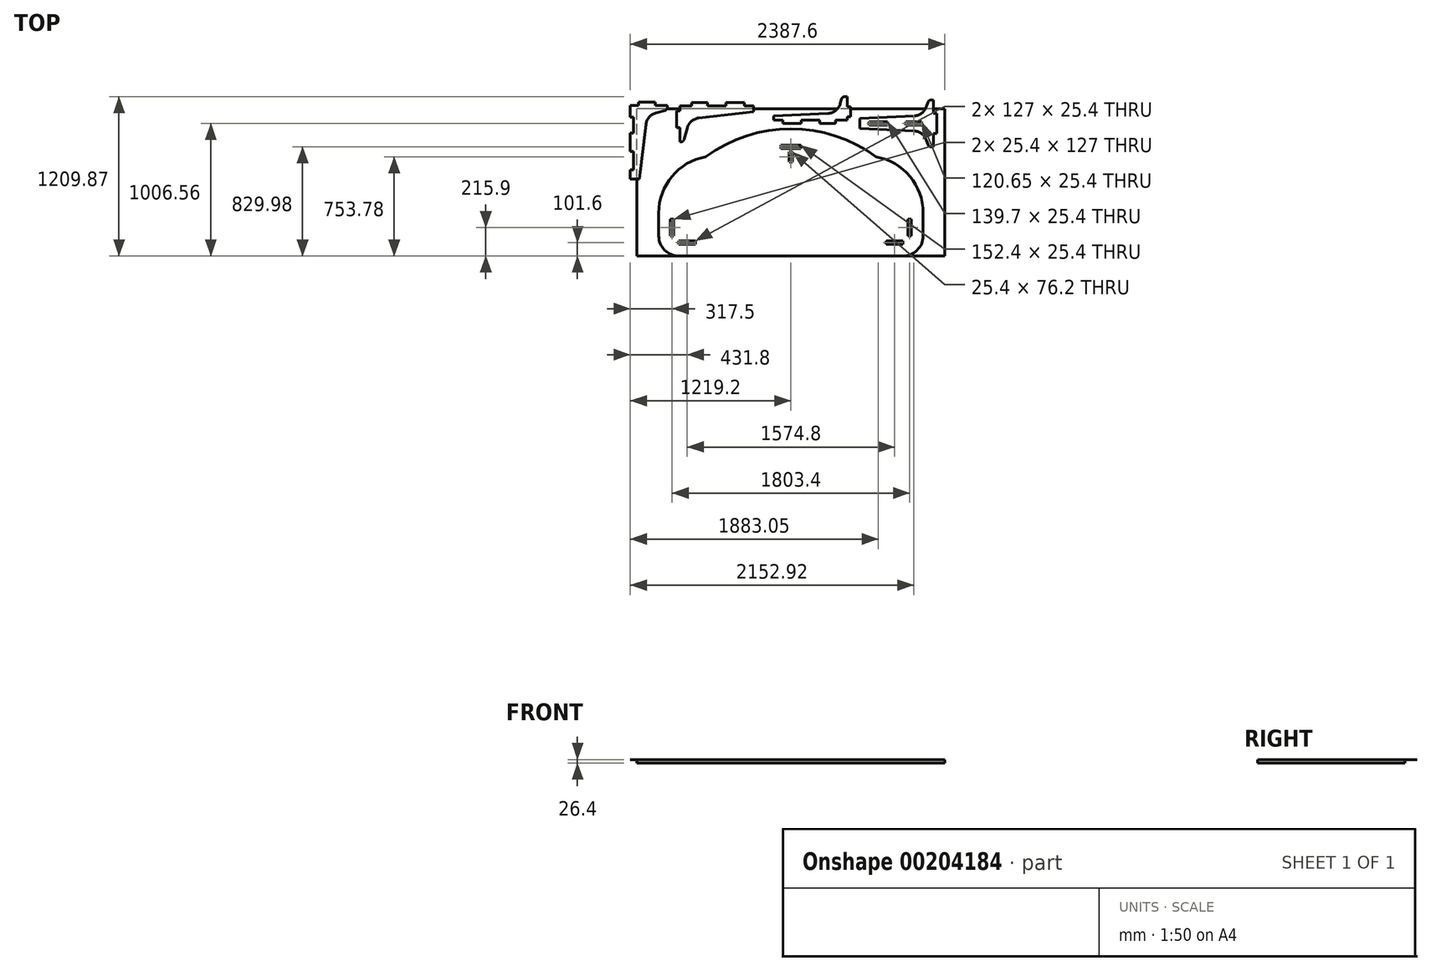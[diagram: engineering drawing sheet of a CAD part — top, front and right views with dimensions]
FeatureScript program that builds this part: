
annotation { "Feature Type Name" : "Feature", "Feature Type Description" : "" }
export const myFeature = defineFeature(function(context is Context, id is Id, definition is map)
    precondition{}
    {
        {
            assignVariable(context, id + "F0", {"name" : "t", "anyValue" : 1});
        }
        {
            var Q0;
            Q0=qCreatedBy(makeId("Top.planeOp"),FACE);
            var sketch = newSketch(context, id + "F1", { "sketchPlane" : qUnion([Q0])});
            skLineSegment(sketch, "E0.left", {"start": v(1219.2, 609.6) * mm, "end": v(1219.2, -609.6) * mm, "construction": true});
            skPoint(sketch, "E0.middle", {"position": v(0, 0) * mm});
            skArc(sketch, "E1", {"start": v(-647.7, 193.56) * mm, "mid": v(-902.68, 45.62) * mm, "end": v(-1003.3, -231.47) * mm});
            skArc(sketch, "E2.MirrorCS", {"start": v(647.7, 193.56) * mm, "mid": v(902.68, 45.62) * mm, "end": v(1003.3, -231.47) * mm});
            skLineSegment(sketch, "E3", {"start": v(-1003.3, -231.47) * mm, "end": v(-1003.3, -406.4) * mm});
            skLineSegment(sketch, "E4", {"start": v(-850.9, -558.8) * mm, "end": v(850.9, -558.8) * mm});
            skLineSegment(sketch, "E5", {"start": v(1003.3, -406.4) * mm, "end": v(1003.3, -231.47) * mm});
            skPoint(sketch, "E6.visualSharp", {"position": v(-850.9, -558.8) * mm});
            skArc(sketch, "E6.filletArc", {"start": v(-1003.3, -406.4) * mm, "mid": v(-958.66, -514.16) * mm, "end": v(-850.9, -558.8) * mm});
            skPoint(sketch, "E7.visualSharp", {"position": v(1003.3, -558.8) * mm});
            skArc(sketch, "E7.filletArc", {"start": v(850.9, -558.8) * mm, "mid": v(958.66, -514.16) * mm, "end": v(1003.3, -406.4) * mm});
            skLineSegment(sketch, "E8", {"start": v(-1219.2, 584.2) * mm, "end": v(-1155.7, 584.2) * mm});
            skLineSegment(sketch, "E9", {"start": v(-1155.7, 584.2) * mm, "end": v(-1155.7, 609.6) * mm});
            skLineSegment(sketch, "E10", {"start": v(-1155.7, 609.6) * mm, "end": v(-1028.7, 609.6) * mm});
            skLineSegment(sketch, "E11", {"start": v(-1028.7, 609.6) * mm, "end": v(-1028.7, 584.2) * mm});
            skLineSegment(sketch, "E12", {"start": v(-1028.7, 584.2) * mm, "end": v(-936.24, 584.2) * mm});
            skLineSegment(sketch, "E13", {"start": v(-936.24, 584.2) * mm, "end": v(-936.24, 571.07) * mm});
            skLineSegment(sketch, "E14", {"start": v(-954.77, 546.61) * mm, "end": v(-1026.75, 526.39) * mm});
            skLineSegment(sketch, "E15", {"start": v(-1100.17, 440.49) * mm, "end": v(-1149.15, 25.4) * mm});
            skLineSegment(sketch, "E16", {"start": v(-1149.15, 25.4) * mm, "end": v(-1219.2, 25.4) * mm});
            skPoint(sketch, "E17.visualSharp", {"position": v(-1092.2, 508) * mm});
            skArc(sketch, "E17.filletArc", {"start": v(-1026.75, 526.39) * mm, "mid": v(-1076.5, 494.59) * mm, "end": v(-1100.17, 440.49) * mm});
            skPoint(sketch, "E18", {"position": v(-903.23, 193.63) * mm});
            skPoint(sketch, "E19.MirrorP", {"position": v(903.23, 193.63) * mm});
            skPoint(sketch, "E20", {"position": v(973.65, -544.19) * mm});
            skArc(sketch, "E21", {"start": v(647.7, 193.56) * mm, "mid": v(0, 406.4) * mm, "end": v(-647.7, 193.56) * mm});
            skPoint(sketch, "E22", {"position": v(0, 406.4) * mm});
            skLineSegment(sketch, "E23.bottom", {"start": v(-1219.2, 495.3) * mm, "end": v(-1193.8, 495.3) * mm});
            skLineSegment(sketch, "E23.top", {"start": v(-1219.2, 374.65) * mm, "end": v(-1193.8, 374.65) * mm});
            skLineSegment(sketch, "E23.right", {"start": v(-1193.8, 495.3) * mm, "end": v(-1193.8, 374.65) * mm});
            skLineSegment(sketch, "E24.bottom", {"start": v(-1219.2, 234.95) * mm, "end": v(-1193.8, 234.95) * mm});
            skLineSegment(sketch, "E24.top", {"start": v(-1219.2, 95.25) * mm, "end": v(-1193.8, 95.25) * mm});
            skLineSegment(sketch, "E24.right", {"start": v(-1193.8, 234.95) * mm, "end": v(-1193.8, 95.25) * mm});
            skLineSegment(sketch, "E25", {"start": v(-835.7, 307.22) * mm, "end": v(-843.95, 307.22) * mm});
            skLineSegment(sketch, "E26", {"start": v(-843.95, 307.22) * mm, "end": v(-843.95, 417.08) * mm});
            skLineSegment(sketch, "E27", {"start": v(-843.95, 417.08) * mm, "end": v(-869.35, 417.08) * mm});
            skLineSegment(sketch, "E28", {"start": v(-869.35, 417.08) * mm, "end": v(-869.35, 544.08) * mm});
            skLineSegment(sketch, "E29", {"start": v(-869.35, 544.08) * mm, "end": v(-843.95, 544.08) * mm});
            skLineSegment(sketch, "E30", {"start": v(-843.95, 544.08) * mm, "end": v(-843.95, 582.18) * mm});
            skLineSegment(sketch, "E31", {"start": v(-843.95, 582.18) * mm, "end": v(-755.05, 582.18) * mm});
            skLineSegment(sketch, "E32", {"start": v(-755.05, 582.18) * mm, "end": v(-755.05, 607.58) * mm});
            skLineSegment(sketch, "E33", {"start": v(-755.05, 607.58) * mm, "end": v(-634.4, 607.58) * mm});
            skLineSegment(sketch, "E34", {"start": v(-634.4, 607.58) * mm, "end": v(-634.4, 582.18) * mm});
            skLineSegment(sketch, "E35", {"start": v(-634.4, 582.18) * mm, "end": v(-494.7, 582.18) * mm});
            skLineSegment(sketch, "E36", {"start": v(-494.7, 582.18) * mm, "end": v(-494.7, 607.58) * mm});
            skLineSegment(sketch, "E37", {"start": v(-494.7, 607.58) * mm, "end": v(-355, 607.58) * mm});
            skLineSegment(sketch, "E38", {"start": v(-355, 607.58) * mm, "end": v(-355, 582.18) * mm});
            skLineSegment(sketch, "E39", {"start": v(-355, 582.18) * mm, "end": v(-285.15, 582.18) * mm});
            skLineSegment(sketch, "E40", {"start": v(-285.15, 582.18) * mm, "end": v(-285.15, 537.54) * mm});
            skLineSegment(sketch, "E41", {"start": v(-285.15, 537.54) * mm, "end": v(-700.23, 488.55) * mm});
            skLineSegment(sketch, "E42", {"start": v(-786.14, 415.13) * mm, "end": v(-811.25, 325.75) * mm});
            skLineSegment(sketch, "E43", {"start": v(-1219.2, 584.2) * mm, "end": v(-1219.2, 495.3) * mm});
            skLineSegment(sketch, "E44", {"start": v(-1219.2, 374.65) * mm, "end": v(-1219.2, 234.95) * mm});
            skLineSegment(sketch, "E45", {"start": v(-1219.2, 95.25) * mm, "end": v(-1219.2, 25.4) * mm});
            skLineSegment(sketch, "E46", {"start": v(-285.15, 537.54) * mm, "end": v(-285.15, 607.58) * mm, "construction": true});
            skPoint(sketch, "E47", {"position": v(-914.4, -469.9) * mm});
            skLineSegment(sketch, "E48.bottom", {"start": v(-914.4, -469.9) * mm, "end": v(-850.9, -469.9) * mm, "construction": true});
            skLineSegment(sketch, "E48.top", {"start": v(-914.4, -444.5) * mm, "end": v(-850.9, -444.5) * mm, "construction": true});
            skLineSegment(sketch, "E48.left", {"start": v(-914.4, -469.9) * mm, "end": v(-914.4, -444.5) * mm, "construction": true});
            skLineSegment(sketch, "E49.bottom", {"start": v(-850.9, -469.9) * mm, "end": v(-723.9, -469.9) * mm});
            skLineSegment(sketch, "E49.top", {"start": v(-850.9, -444.5) * mm, "end": v(-723.9, -444.5) * mm});
            skLineSegment(sketch, "E49.left", {"start": v(-850.9, -469.9) * mm, "end": v(-850.9, -444.5) * mm});
            skLineSegment(sketch, "E49.right", {"start": v(-723.9, -469.9) * mm, "end": v(-723.9, -444.5) * mm});
            skLineSegment(sketch, "E50.bottom", {"start": v(-723.9, -469.9) * mm, "end": v(-631.44, -469.9) * mm, "construction": true});
            skLineSegment(sketch, "E50.top", {"start": v(-723.9, -444.5) * mm, "end": v(-631.44, -444.5) * mm, "construction": true});
            skLineSegment(sketch, "E50.left", {"start": v(-723.9, -469.9) * mm, "end": v(-723.9, -444.5) * mm, "construction": true});
            skLineSegment(sketch, "E50.right", {"start": v(-631.44, -469.9) * mm, "end": v(-631.44, -444.5) * mm, "construction": true});
            skLineSegment(sketch, "E51.bottom", {"start": v(-914.4, -406.4) * mm, "end": v(-889, -406.4) * mm});
            skLineSegment(sketch, "E51.top", {"start": v(-914.4, -279.4) * mm, "end": v(-889, -279.4) * mm});
            skLineSegment(sketch, "E51.left", {"start": v(-914.4, -406.4) * mm, "end": v(-914.4, -279.4) * mm});
            skLineSegment(sketch, "E51.right", {"start": v(-889, -406.4) * mm, "end": v(-889, -279.4) * mm});
            skLineSegment(sketch, "E52.bottom", {"start": v(-914.4, -279.4) * mm, "end": v(-889, -279.4) * mm, "construction": true});
            skLineSegment(sketch, "E52.top", {"start": v(-914.4, -169.54) * mm, "end": v(-889, -169.54) * mm, "construction": true});
            skLineSegment(sketch, "E52.left", {"start": v(-914.4, -279.4) * mm, "end": v(-914.4, -169.54) * mm, "construction": true});
            skLineSegment(sketch, "E52.right", {"start": v(-889, -279.4) * mm, "end": v(-889, -169.54) * mm, "construction": true});
            skLineSegment(sketch, "E53.bottom", {"start": v(-914.4, -469.9) * mm, "end": v(-889, -469.9) * mm, "construction": true});
            skLineSegment(sketch, "E53.left", {"start": v(-914.4, -469.9) * mm, "end": v(-914.4, -406.4) * mm, "construction": true});
            skLineSegment(sketch, "E53.right", {"start": v(-889, -469.9) * mm, "end": v(-889, -406.4) * mm, "construction": true});
            skLineSegment(sketch, "E54", {"start": v(-869.35, 607.58) * mm, "end": v(-869.35, 544.08) * mm, "construction": true});
            skPoint(sketch, "E55.visualSharp", {"position": v(-767.75, 480.58) * mm});
            skArc(sketch, "E55.filletArc", {"start": v(-700.23, 488.55) * mm, "mid": v(-754.34, 464.88) * mm, "end": v(-786.14, 415.13) * mm});
            skLineSegment(sketch, "E56", {"start": v(1082.95, 447.76) * mm, "end": v(524.15, 447.76) * mm, "construction": true});
            skLineSegment(sketch, "E57", {"start": v(1082.95, 447.76) * mm, "end": v(1082.95, 625.56) * mm, "construction": true});
            skLineSegment(sketch, "E58.MirrorCS", {"start": v(1082.95, 447.76) * mm, "end": v(1082.95, 269.96) * mm, "construction": true});
            skLineSegment(sketch, "E59", {"start": v(524.15, 447.76) * mm, "end": v(524.15, 485.86) * mm});
            skLineSegment(sketch, "E60", {"start": v(524.15, 485.86) * mm, "end": v(936.7, 505.42) * mm});
            skLineSegment(sketch, "E61", {"start": v(1028.49, 575.4) * mm, "end": v(1039.13, 608.04) * mm});
            skLineSegment(sketch, "E62", {"start": v(1063.28, 625.56) * mm, "end": v(1082.95, 625.56) * mm});
            skPoint(sketch, "E63.visualSharp", {"position": v(1006.75, 508.75) * mm});
            skArc(sketch, "E63.filletArc", {"start": v(936.7, 505.42) * mm, "mid": v(993.5, 526.12) * mm, "end": v(1028.49, 575.4) * mm});
            skArc(sketch, "E64.MirrorCS", {"start": v(936.7, 390.1) * mm, "mid": v(993.5, 369.4) * mm, "end": v(1028.49, 320.11) * mm});
            skLineSegment(sketch, "E65.MirrorCS", {"start": v(1063.28, 269.96) * mm, "end": v(1082.95, 269.96) * mm});
            skLineSegment(sketch, "E66.MirrorCS", {"start": v(1028.49, 320.11) * mm, "end": v(1039.13, 287.48) * mm});
            skPoint(sketch, "E67.MirrorP", {"position": v(1006.75, 386.77) * mm});
            skLineSegment(sketch, "E68.MirrorCS", {"start": v(524.15, 409.66) * mm, "end": v(936.7, 390.1) * mm});
            skLineSegment(sketch, "E69.MirrorCS", {"start": v(524.15, 447.76) * mm, "end": v(524.15, 409.66) * mm});
            skLineSegment(sketch, "E70", {"start": v(1082.95, 625.56) * mm, "end": v(1082.95, 523.96) * mm});
            skLineSegment(sketch, "E71", {"start": v(1082.95, 523.96) * mm, "end": v(1108.35, 523.96) * mm});
            skLineSegment(sketch, "E72", {"start": v(1108.35, 523.96) * mm, "end": v(1108.35, 447.76) * mm});
            skLineSegment(sketch, "E73.MirrorCS", {"start": v(1082.95, 371.56) * mm, "end": v(1108.35, 371.56) * mm});
            skLineSegment(sketch, "E74.MirrorCS", {"start": v(1108.35, 371.56) * mm, "end": v(1108.35, 447.76) * mm});
            skLineSegment(sketch, "E75.MirrorCS", {"start": v(1082.95, 269.96) * mm, "end": v(1082.95, 371.56) * mm});
            skLineSegment(sketch, "E76", {"start": v(-1193.8, 25.4) * mm, "end": v(-1193.8, 584.2) * mm, "construction": true});
            skLineSegment(sketch, "E77.bottom", {"start": v(1003.3, -558.8) * mm, "end": v(-850.9, -558.8) * mm, "construction": true});
            skLineSegment(sketch, "E77.right", {"start": v(-850.9, -558.8) * mm, "end": v(-850.9, 509.6) * mm, "construction": true});
            skLineSegment(sketch, "E78", {"start": v(-1219.2, -609.6) * mm, "end": v(1219.2, -609.6) * mm, "construction": true});
            skLineSegment(sketch, "E79", {"start": v(-1219.2, 25.4) * mm, "end": v(-1219.2, 609.6) * mm, "construction": true});
            skLineSegment(sketch, "E80", {"start": v(-1219.2, 609.6) * mm, "end": v(-936.24, 609.6) * mm, "construction": true});
            skArc(sketch, "E81.0", {"start": v(-1028.7, -406.4) * mm, "mid": v(-976.62, -532.12) * mm, "end": v(-850.9, -584.2) * mm, "construction": true});
            skLineSegment(sketch, "E81.1", {"start": v(-1028.7, -231.47) * mm, "end": v(-1028.7, -406.4) * mm, "construction": true});
            skArc(sketch, "E81.2", {"start": v(-658.04, 217.47) * mm, "mid": v(-924.06, 59.62) * mm, "end": v(-1028.7, -231.47) * mm, "construction": true});
            skArc(sketch, "E81.3", {"start": v(850.9, -584.2) * mm, "mid": v(976.62, -532.12) * mm, "end": v(1028.7, -406.4) * mm, "construction": true});
            skLineSegment(sketch, "E81.4", {"start": v(1028.7, -406.4) * mm, "end": v(1028.7, -231.47) * mm, "construction": true});
            skArc(sketch, "E81.5", {"start": v(658.04, 217.47) * mm, "mid": v(924.06, 59.62) * mm, "end": v(1028.7, -231.47) * mm, "construction": true});
            skArc(sketch, "E81.6", {"start": v(658.04, 217.47) * mm, "mid": v(0, 431.8) * mm, "end": v(-658.04, 217.47) * mm, "construction": true});
            skLineSegment(sketch, "E82.bottom", {"start": v(1168.4, -558.8) * mm, "end": v(-1168.4, -558.8) * mm, "construction": true});
            skLineSegment(sketch, "E82.left", {"start": v(1168.4, -558.8) * mm, "end": v(1168.4, 558.8) * mm, "construction": true});
            skLineSegment(sketch, "E83", {"start": v(0, 406.4) * mm, "end": v(0, -558.8) * mm, "construction": true});
            skLineSegment(sketch, "E84.MirrorCS", {"start": v(850.9, -469.9) * mm, "end": v(723.9, -469.9) * mm});
            skLineSegment(sketch, "E85.MirrorCS", {"start": v(723.9, -469.9) * mm, "end": v(723.9, -444.5) * mm});
            skLineSegment(sketch, "E86.MirrorCS", {"start": v(850.9, -444.5) * mm, "end": v(723.9, -444.5) * mm});
            skLineSegment(sketch, "E87.MirrorCS", {"start": v(850.9, -469.9) * mm, "end": v(850.9, -444.5) * mm});
            skLineSegment(sketch, "E88.MirrorCS", {"start": v(914.4, -406.4) * mm, "end": v(889, -406.4) * mm});
            skLineSegment(sketch, "E89.MirrorCS", {"start": v(889, -406.4) * mm, "end": v(889, -279.4) * mm});
            skLineSegment(sketch, "E90.MirrorCS", {"start": v(914.4, -406.4) * mm, "end": v(914.4, -279.4) * mm});
            skLineSegment(sketch, "E91.MirrorCS", {"start": v(914.4, -279.4) * mm, "end": v(889, -279.4) * mm});
            skArc(sketch, "E92.1.0.0", {"start": v(281.65, 523.93) * mm, "mid": v(340.5, 546.32) * mm, "end": v(374.86, 599.1) * mm});
            skLineSegment(sketch, "E92.1.0.1", {"start": v(408.28, 651.07) * mm, "end": v(427.95, 651.07) * mm});
            skLineSegment(sketch, "E92.1.0.2", {"start": v(-130.85, 473.16) * mm, "end": v(-130.9, 503.93) * mm});
            skPoint(sketch, "E92.1.0.3", {"position": v(264.16, 508.75) * mm});
            skLineSegment(sketch, "E92.1.0.4", {"start": v(453.35, 574.87) * mm, "end": v(453.35, 498.67) * mm});
            skLineSegment(sketch, "E92.1.0.5", {"start": v(-130.9, 503.93) * mm, "end": v(281.65, 523.93) * mm});
            skLineSegment(sketch, "E92.1.0.8", {"start": v(427.95, 574.87) * mm, "end": v(427.95, 651.07) * mm});
            skLineSegment(sketch, "E92.1.0.9", {"start": v(427.95, 574.87) * mm, "end": v(453.35, 574.87) * mm});
            skLineSegment(sketch, "E92.1.0.10", {"start": v(374.86, 599.1) * mm, "end": v(383.75, 632.24) * mm});
            skLineSegment(sketch, "E93", {"start": v(453.35, 498.67) * mm, "end": v(427.95, 498.67) * mm});
            skLineSegment(sketch, "E94", {"start": v(427.95, 498.67) * mm, "end": v(427.95, 473.27) * mm});
            skLineSegment(sketch, "E95.top", {"start": v(-130.85, 447.76) * mm, "end": v(427.95, 447.76) * mm, "construction": true});
            skLineSegment(sketch, "E95.left", {"start": v(-130.85, 473.16) * mm, "end": v(-130.85, 447.76) * mm, "construction": true});
            skLineSegment(sketch, "E95.right", {"start": v(427.95, 473.27) * mm, "end": v(427.95, 447.76) * mm, "construction": true});
            skLineSegment(sketch, "E96", {"start": v(339.05, 473.27) * mm, "end": v(339.05, 447.76) * mm});
            skLineSegment(sketch, "E97", {"start": v(339.05, 447.76) * mm, "end": v(218.4, 447.76) * mm});
            skLineSegment(sketch, "E98", {"start": v(218.4, 447.76) * mm, "end": v(218.4, 473.27) * mm});
            skLineSegment(sketch, "E99", {"start": v(218.4, 473.27) * mm, "end": v(78.7, 473.27) * mm});
            skLineSegment(sketch, "E100", {"start": v(78.7, 473.27) * mm, "end": v(78.7, 447.76) * mm});
            skLineSegment(sketch, "E101", {"start": v(78.7, 447.76) * mm, "end": v(-61, 447.76) * mm});
            skLineSegment(sketch, "E102", {"start": v(-61, 447.76) * mm, "end": v(-61, 473.27) * mm});
            skLineSegment(sketch, "E103", {"start": v(-61, 473.27) * mm, "end": v(-130.85, 473.16) * mm});
            skLineSegment(sketch, "E104", {"start": v(339.05, 473.27) * mm, "end": v(427.95, 473.27) * mm});
            skLineSegment(sketch, "E105.bottom", {"start": v(733.7, 460.46) * mm, "end": v(594, 460.46) * mm});
            skLineSegment(sketch, "E105.top", {"start": v(733.7, 435.06) * mm, "end": v(594, 435.06) * mm});
            skLineSegment(sketch, "E105.left", {"start": v(733.7, 460.46) * mm, "end": v(733.7, 435.06) * mm});
            skLineSegment(sketch, "E105.right", {"start": v(594, 460.46) * mm, "end": v(594, 435.06) * mm});
            skPoint(sketch, "E105.middle", {"position": v(663.85, 447.76) * mm});
            skLineSegment(sketch, "E106.bottom", {"start": v(873.4, 435.06) * mm, "end": v(994.05, 435.06) * mm});
            skLineSegment(sketch, "E106.top", {"start": v(873.4, 460.46) * mm, "end": v(994.05, 460.46) * mm});
            skLineSegment(sketch, "E106.left", {"start": v(873.4, 435.06) * mm, "end": v(873.4, 460.46) * mm});
            skLineSegment(sketch, "E106.right", {"start": v(994.05, 435.06) * mm, "end": v(994.05, 460.46) * mm});
            skPoint(sketch, "E106.middle", {"position": v(933.72, 447.76) * mm});
            skLineSegment(sketch, "E107", {"start": v(594, 460.46) * mm, "end": v(524.15, 460.46) * mm, "construction": true});
            skPoint(sketch, "E107.endSnap0", {"position": v(524.15, 466.81) * mm});
            skLineSegment(sketch, "E108", {"start": v(873.4, 460.46) * mm, "end": v(733.7, 460.46) * mm, "construction": true});
            skLineSegment(sketch, "E109.bottom", {"start": v(-76.2, 258.48) * mm, "end": v(76.2, 258.48) * mm});
            skLineSegment(sketch, "E109.top", {"start": v(-76.2, 283.88) * mm, "end": v(76.2, 283.88) * mm});
            skLineSegment(sketch, "E109.left", {"start": v(-76.2, 258.48) * mm, "end": v(-76.2, 283.88) * mm});
            skLineSegment(sketch, "E109.right", {"start": v(76.2, 258.48) * mm, "end": v(76.2, 283.88) * mm});
            skPoint(sketch, "E109.middle", {"position": v(0, 271.18) * mm});
            skLineSegment(sketch, "E110.bottom", {"start": v(-12.7, 156.88) * mm, "end": v(12.7, 156.88) * mm});
            skLineSegment(sketch, "E110.top", {"start": v(-12.7, 233.08) * mm, "end": v(12.7, 233.08) * mm});
            skLineSegment(sketch, "E110.left", {"start": v(-12.7, 156.88) * mm, "end": v(-12.7, 233.08) * mm});
            skLineSegment(sketch, "E110.right", {"start": v(12.7, 156.88) * mm, "end": v(12.7, 233.08) * mm});
            skPoint(sketch, "E110.middle", {"position": v(0, 194.98) * mm});
            skLineSegment(sketch, "E111", {"start": v(1130.56, 523.96) * mm, "end": v(1130.56, 371.56) * mm, "construction": true});
            skPoint(sketch, "E112.visualSharp", {"position": v(-936.24, 551.82) * mm});
            skArc(sketch, "E112.filletArc", {"start": v(-954.77, 546.61) * mm, "mid": v(-941.4, 555.73) * mm, "end": v(-936.24, 571.07) * mm});
            skPoint(sketch, "E113.visualSharp", {"position": v(-816.46, 307.22) * mm});
            skArc(sketch, "E113.filletArc", {"start": v(-835.7, 307.22) * mm, "mid": v(-820.37, 312.37) * mm, "end": v(-811.25, 325.75) * mm});
            skPoint(sketch, "E114.visualSharp", {"position": v(1044.85, 625.56) * mm});
            skArc(sketch, "E114.filletArc", {"start": v(1063.28, 625.56) * mm, "mid": v(1048.36, 620.72) * mm, "end": v(1039.13, 608.04) * mm});
            skPoint(sketch, "E115.visualSharp", {"position": v(1044.85, 269.96) * mm});
            skArc(sketch, "E115.filletArc", {"start": v(1039.13, 287.48) * mm, "mid": v(1048.36, 274.8) * mm, "end": v(1063.28, 269.96) * mm});
            skPoint(sketch, "E116.visualSharp", {"position": v(388.8, 651.07) * mm});
            skArc(sketch, "E116.filletArc", {"start": v(408.28, 651.07) * mm, "mid": v(392.82, 645.82) * mm, "end": v(383.75, 632.24) * mm});
            skLineSegment(sketch, "E117", {"start": v(12.7, 233.08) * mm, "end": v(12.7, 258.48) * mm, "construction": true});
            skLineSegment(sketch, "E118.bottom", {"start": v(-1092.2, 508) * mm, "end": v(-1219.2, 508) * mm, "construction": true});
            skLineSegment(sketch, "E118.top", {"start": v(-1092.2, 584.2) * mm, "end": v(-1219.2, 584.2) * mm, "construction": true});
            skLineSegment(sketch, "E118.left", {"start": v(-1092.2, 508) * mm, "end": v(-1092.2, 584.2) * mm, "construction": true});
            skLineSegment(sketch, "E118.right", {"start": v(-1219.2, 508) * mm, "end": v(-1219.2, 584.2) * mm, "construction": true});
            skLineSegment(sketch, "E119.bottom", {"start": v(-767.75, 480.58) * mm, "end": v(-843.95, 480.58) * mm, "construction": true});
            skLineSegment(sketch, "E119.top", {"start": v(-767.75, 607.58) * mm, "end": v(-843.95, 607.58) * mm, "construction": true});
            skLineSegment(sketch, "E119.left", {"start": v(-767.75, 480.58) * mm, "end": v(-767.75, 607.58) * mm, "construction": true});
            skLineSegment(sketch, "E119.right", {"start": v(-843.95, 480.58) * mm, "end": v(-843.95, 607.58) * mm, "construction": true});
            skLineSegment(sketch, "E120", {"start": v(-843.95, 607.58) * mm, "end": v(-285.15, 607.58) * mm, "construction": true});
            skLineSegment(sketch, "E121", {"start": v(-1026.75, 526.39) * mm, "end": v(-1026.75, 584.2) * mm, "construction": true});
            skLineSegment(sketch, "E122", {"start": v(-1100.17, 440.49) * mm, "end": v(-1219.2, 440.49) * mm, "construction": true});
            skLineSegment(sketch, "E123", {"start": v(-700.23, 488.55) * mm, "end": v(-700.23, 607.58) * mm, "construction": true});
            skLineSegment(sketch, "E124", {"start": v(-786.14, 415.13) * mm, "end": v(-843.95, 415.13) * mm, "construction": true});
            skLineSegment(sketch, "E125", {"start": v(427.95, 473.27) * mm, "end": v(427.95, 651.07) * mm, "construction": true});
            skSolve(sketch);
        }
        {
            var Q0;
            Q0=makeQuery(id+"F1.imprint","IMPRINT",FACE,{"disambiguationData":[TD([[makeQuery(id+"F1.imprint","IMPRINT",EDGE,{"derivedFrom":sQuery(id+"F1.wireOp",EDGE,"E1")}),1.0]])]});
            var Q1;
            Q1=makeQuery(id+"F1.imprint","IMPRINT",FACE,{"disambiguationData":[TD([[makeQuery(id+"F1.imprint","IMPRINT",EDGE,{"derivedFrom":sQuery(id+"F1.wireOp",EDGE,"E8")}),-1.0]])]});
            var Q2;
            Q2=makeQuery(id+"F1.imprint","IMPRINT",FACE,{"disambiguationData":[TD([[makeQuery(id+"F1.imprint","IMPRINT",EDGE,{"derivedFrom":sQuery(id+"F1.wireOp",EDGE,"E25")}),-1.0]])]});
            var Q3;
            Q3=makeQuery(id+"F1.imprint","IMPRINT",FACE,{"disambiguationData":[TD([[makeQuery(id+"F1.imprint","IMPRINT",EDGE,{"derivedFrom":sQuery(id+"F1.wireOp",EDGE,"E59")}),-1.0]])]});
            var Q4;
            Q4=makeQuery(id+"F1.imprint","IMPRINT",FACE,{"disambiguationData":[TD([[makeQuery(id+"F1.imprint","IMPRINT",EDGE,{"derivedFrom":sQuery(id+"F1.wireOp",EDGE,"E92.1.0.0")}),-1.0]])]});
            extrude(context, id + "F2", {"entities" : qUnion([Q0, Q1, Q2, Q3, Q4]), "depth" : (getVariable(context, 't')) * mm});
        }
        {
            var Q0;
            Q0=makeQuery(id+"F1.imprint","IMPRINT",FACE,{"disambiguationData":[TD([[makeQuery(id+"F1.imprint","IMPRINT",EDGE,{"derivedFrom":sQuery(id+"F1.wireOp",EDGE,"E1")}),1.0]])]});
            var sketch = newSketch(context, id + "F3", { "sketchPlane" : qUnion([Q0])});
            skLineSegment(sketch, "E126.0", {"start": v(1168.4, -558.8) * mm, "end": v(-1168.4, -558.8) * mm});
            skLineSegment(sketch, "E126.1", {"start": v(-1168.4, -558.8) * mm, "end": v(-1168.4, 558.8) * mm});
            skLineSegment(sketch, "E126.2", {"start": v(1168.4, -558.8) * mm, "end": v(1168.4, 558.8) * mm});
            skLineSegment(sketch, "E126.3", {"start": v(1168.4, 558.8) * mm, "end": v(-1168.4, 558.8) * mm});
            skSolve(sketch);
        }
        {
            var Q0;
            Q0 = qSketchRegion(id + "F3", true);
            extrude(context, id + "F4", {"entities" : qUnion([Q0]), "oppositeDirection" : true, "depth" : 25.4 * mm});
        }
    });
